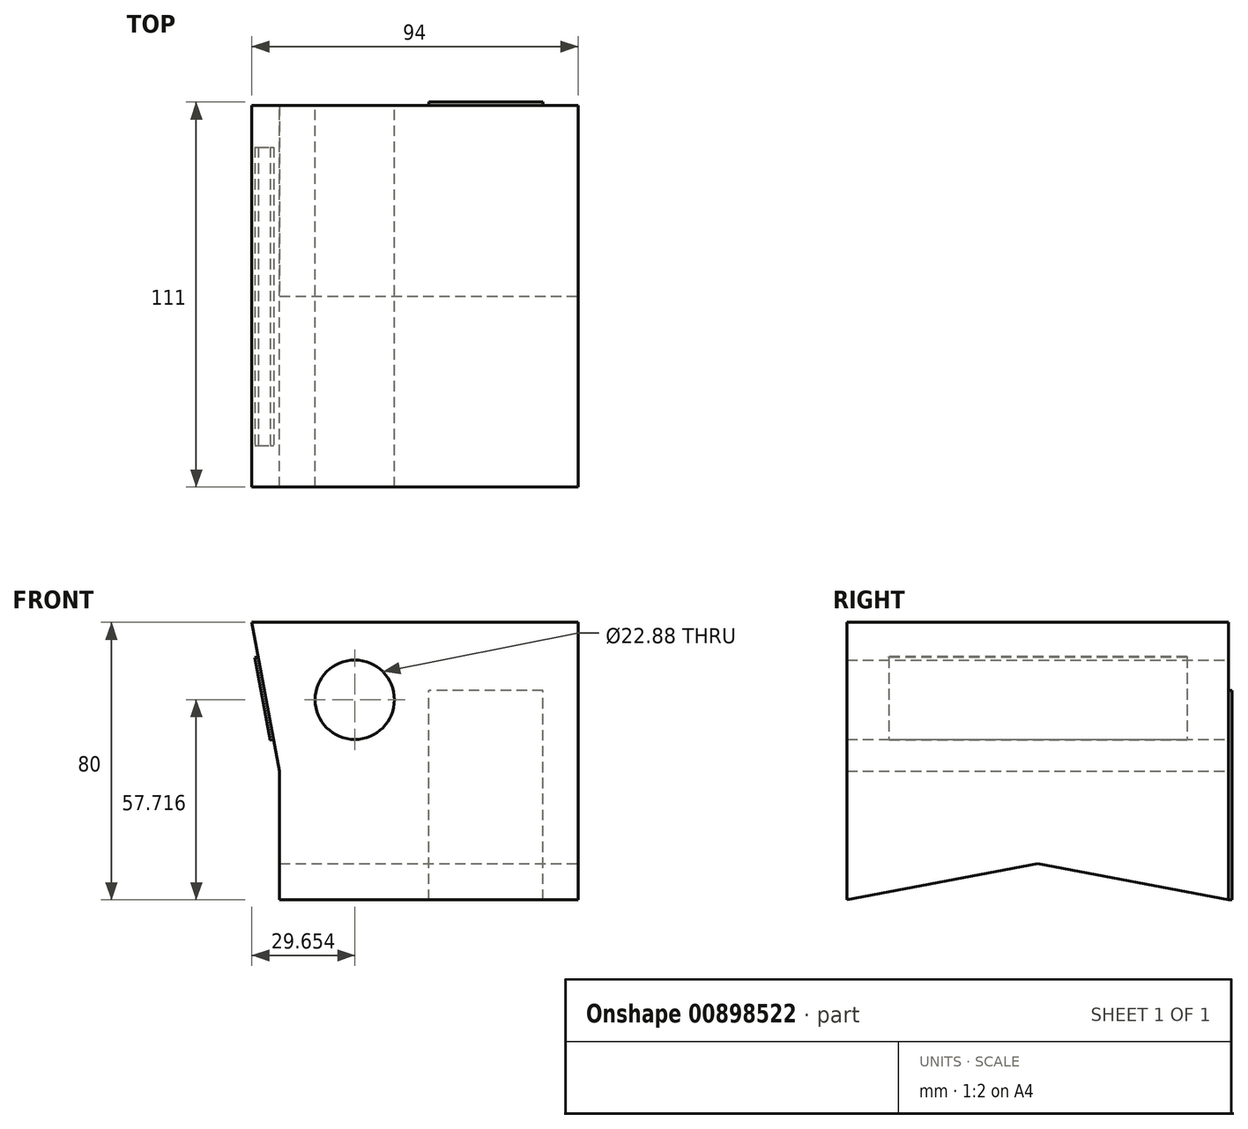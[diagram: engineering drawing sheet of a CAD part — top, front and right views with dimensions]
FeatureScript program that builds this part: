
annotation { "Feature Type Name" : "Feature", "Feature Type Description" : "" }
export const myFeature = defineFeature(function(context is Context, id is Id, definition is map)
    precondition{}
    {
        {
            var Q0;
            Q0=qCreatedBy(makeId("Front.planeOp"),FACE);
            var sketch = newSketch(context, id + "F0", { "sketchPlane" : qUnion([Q0])});
            skLineSegment(sketch, "E0.bottom", {"start": v(0, 0) * mm, "end": v(-80, 0) * mm});
            skLineSegment(sketch, "E0.top", {"start": v(0, 80) * mm, "end": v(-80, 80) * mm});
            skLineSegment(sketch, "E0.left", {"start": v(0, 0) * mm, "end": v(0, 80) * mm});
            skLineSegment(sketch, "E0.right", {"start": v(-80, 0) * mm, "end": v(-80, 80) * mm});
            skLineSegment(sketch, "E1", {"start": v(-80, 80) * mm, "end": v(-88, 80) * mm});
            skLineSegment(sketch, "E2", {"start": v(-88, 80) * mm, "end": v(-80, 37.1) * mm});
            skSolve(sketch);
        }
        {
            var Q0;
            {var subQ0=sQuery(id+"F0.wireOp",EDGE,"E1");Q0=makeQuery(id+"F0.imprint","IMPRINT",FACE,{"disambiguationData":[TD([[makeQuery(id+"F0.imprint","IMPRINT",EDGE,{"derivedFrom":subQ0}),1.0]])]});}
            var Q1;
            {var subQ1=sQuery(id+"F0.wireOp",EDGE,"E0.bottom");Q1=makeQuery(id+"F0.imprint","IMPRINT",FACE,{"disambiguationData":[TD([[makeQuery(id+"F0.imprint","IMPRINT",EDGE,{"derivedFrom":subQ1}),-1.0]])]});}
            extrude(context, id + "F1", {"entities" : qUnion([Q0, Q1]), "depth" : 6 * mm, "offsetDistance" : 25 * mm});
        }
        {
            var Q0;
            Q0=makeQuery(id+"F1.opExtrude","SWEPT_FACE",FACE,{"disambiguationData":[OSD([sQuery(id+"F0.wireOp",EDGE,"E0.left")])]});
            var sketch = newSketch(context, id + "F2", { "sketchPlane" : qUnion([Q0])});
            skLineSegment(sketch, "E3.bottom", {"start": v(-6, 0) * mm, "end": v(104, 0) * mm});
            skLineSegment(sketch, "E3.top", {"start": v(-6, 80) * mm, "end": v(104, 80) * mm});
            skLineSegment(sketch, "E3.left", {"start": v(-6, 0) * mm, "end": v(-6, 80) * mm});
            skLineSegment(sketch, "E3.right", {"start": v(104, 0) * mm, "end": v(104, 80) * mm});
            skSolve(sketch);
        }
        {
            var Q0;
            {var subQ2=sQuery(id+"F2.wireOp",EDGE,"E3.right");Q0=makeQuery(id+"F2.imprint","IMPRINT",FACE,{"disambiguationData":[TD([[makeQuery(id+"F2.imprint","IMPRINT",EDGE,{"derivedFrom":subQ2}),1.0]])]});}
            var Q1;
            {var subQ2=sQuery(id+"F2.wireOp",EDGE,"E3.left");Q1=makeQuery(id+"F2.imprint","IMPRINT",FACE,{"disambiguationData":[TD([[makeQuery(id+"F2.imprint","IMPRINT",EDGE,{"derivedFrom":subQ2}),-1.0]])]});}
            extrude(context, id + "F3", {"entities" : qUnion([Q0, Q1]), "operationType" : NewBodyOperationType.ADD, "depth" : 6 * mm, "offsetDistance" : 25 * mm});
        }
        {
            var Q0;
            Q0=makeQuery(id+"F3.boolean.opBoolean","MERGE",FACE,{"derivedFrom":[makeQuery(id+"F1.opExtrude","CAP_FACE",FACE,{"disambiguationData":[OSD([sQuery(id+"F0.wireOp",EDGE,"E0.bottom"),sQuery(id+"F0.wireOp",EDGE,"E0.top"),sQuery(id+"F0.wireOp",EDGE,"E0.left"),sQuery(id+"F0.wireOp",EDGE,"E0.right"),sQuery(id+"F0.wireOp",EDGE,"E1"),sQuery(id+"F0.wireOp",EDGE,"E2")])],"isStart":false}),makeQuery(id+"F3.opExtrude","SWEPT_FACE",FACE,{"disambiguationData":[OSD([sQuery(id+"F2.wireOp",EDGE,"E3.left")])]})]});
            var sketch = newSketch(context, id + "F4", { "sketchPlane" : qUnion([Q0])});
            skLineSegment(sketch, "E4", {"start": v(0, 80) * mm, "end": v(0, 0) * mm});
            skSolve(sketch);
        }
        {
            var Q0;
            Q0=makeQuery(id+"F1.opExtrude","CAP_FACE",FACE,{"disambiguationData":[OSD([sQuery(id+"F0.wireOp",EDGE,"E0.bottom"),sQuery(id+"F0.wireOp",EDGE,"E0.top"),sQuery(id+"F0.wireOp",EDGE,"E0.left"),sQuery(id+"F0.wireOp",EDGE,"E0.right"),sQuery(id+"F0.wireOp",EDGE,"E1"),sQuery(id+"F0.wireOp",EDGE,"E2")])],"isStart":true});
            var Q1;
            Q1=makeQuery(id+"F3.opExtrude","SWEPT_FACE",FACE,{"disambiguationData":[OSD([sQuery(id+"F2.wireOp",EDGE,"E3.right")])]});
            extrude(context, id + "F5", {"entities" : qUnion([Q0]), "operationType" : NewBodyOperationType.ADD, "endBound" : BoundingType.UP_TO_SURFACE, "depth" : 25 * mm, "endBoundEntityFace" : qUnion([Q1]), "offsetDistance" : 25 * mm});
        }
        {
            var Q0;
            Q0=makeQuery(id+"F3.opExtrude","CAP_FACE",FACE,{"disambiguationData":[OSD([sQuery(id+"F2.wireOp",EDGE,"E3.bottom"),sQuery(id+"F2.wireOp",EDGE,"E3.top"),sQuery(id+"F2.wireOp",EDGE,"E3.left"),sQuery(id+"F2.wireOp",EDGE,"E3.right")])],"isStart":false});
            var sketch = newSketch(context, id + "F6", { "sketchPlane" : qUnion([Q0])});
            skLineSegment(sketch, "E5", {"start": v(49, 10.5) * mm, "end": v(104, 0) * mm});
            skLineSegment(sketch, "E6", {"start": v(49, 10.5) * mm, "end": v(-6, 0) * mm});
            skSolve(sketch);
        }
        {
            var Q0;
            Q0=makeQuery(id+"F6.imprint","IMPRINT",FACE,{"disambiguationData":[TD([[makeQuery(id+"F6.imprint","IMPRINT",EDGE,{"derivedFrom":sQuery(id+"F6.wireOp",EDGE,"E5")}),-1.0]])]});
            extrude(context, id + "F7", {"entities" : qUnion([Q0]), "operationType" : NewBodyOperationType.REMOVE, "oppositeDirection" : true, "depth" : 200 * mm, "offsetDistance" : 25 * mm});
        }
        {
            var Q0;
            Q0=makeQuery(id+"F5.boolean.opBoolean","MERGE",FACE,{"derivedFrom":[makeQuery(id+"F3.opExtrude","SWEPT_FACE",FACE,{"disambiguationData":[OSD([sQuery(id+"F2.wireOp",EDGE,"E3.right")])]}),makeQuery(id+"F5.opExtrude","CAP_FACE",FACE,{"disambiguationData":[OSD([sQuery(id+"F0.wireOp",EDGE,"E0.bottom"),sQuery(id+"F0.wireOp",EDGE,"E0.top"),sQuery(id+"F0.wireOp",EDGE,"E0.left"),sQuery(id+"F0.wireOp",EDGE,"E0.right"),sQuery(id+"F0.wireOp",EDGE,"E1"),sQuery(id+"F0.wireOp",EDGE,"E2")])],"isStart":false})]});
            var sketch = newSketch(context, id + "F8", { "sketchPlane" : qUnion([Q0])});
            skLineSegment(sketch, "E7", {"start": v(0, 80) * mm, "end": v(0, 0) * mm});
            skLineSegment(sketch, "E8", {"start": v(85.12, 64.56) * mm, "end": v(79.22, 65.66) * mm});
            skLineSegment(sketch, "E9", {"start": v(79.22, 65.66) * mm, "end": v(81.9, 80) * mm});
            skLineSegment(sketch, "E10", {"start": v(80, 0) * mm, "end": v(74, 0) * mm});
            skLineSegment(sketch, "E11", {"start": v(74, 0) * mm, "end": v(74, 37.65) * mm});
            skLineSegment(sketch, "E12", {"start": v(74, 37.65) * mm, "end": v(81.9, 80) * mm});
            skLineSegment(sketch, "E13.bottom", {"start": v(8.37, 0) * mm, "end": v(39.44, 0) * mm});
            skLineSegment(sketch, "E13.top", {"start": v(8.37, 63.48) * mm, "end": v(39.44, 63.48) * mm});
            skLineSegment(sketch, "E13.left", {"start": v(8.37, 0) * mm, "end": v(8.37, 63.48) * mm});
            skLineSegment(sketch, "E13.right", {"start": v(39.44, 0) * mm, "end": v(39.44, 63.48) * mm});
            skCircle(sketch, "E14", {"center": v(58.35, 57.72) * mm, "radius": 11.44 * mm});
            skSolve(sketch);
        }
        {
            var Q0;
            Q0=makeQuery(id+"F3.opExtrude","CAP_FACE",FACE,{"disambiguationData":[OSD([sQuery(id+"F2.wireOp",EDGE,"E3.bottom"),sQuery(id+"F2.wireOp",EDGE,"E3.top"),sQuery(id+"F2.wireOp",EDGE,"E3.left"),sQuery(id+"F2.wireOp",EDGE,"E3.right")])],"isStart":false});
            var sketch = newSketch(context, id + "F9", { "sketchPlane" : qUnion([Q0])});
            skLineSegment(sketch, "E15.bottom", {"start": v(-6, 80) * mm, "end": v(6, 80) * mm});
            skLineSegment(sketch, "E15.left", {"start": v(-6, 80) * mm, "end": v(-6, 70) * mm});
            skLineSegment(sketch, "E16.bottom", {"start": v(104, 80) * mm, "end": v(92, 80) * mm});
            skLineSegment(sketch, "E16.left", {"start": v(104, 80) * mm, "end": v(104, 70) * mm});
            skLineSegment(sketch, "E17.bottom", {"start": v(5.82, 70) * mm, "end": v(92, 70) * mm});
            skLineSegment(sketch, "E17.top", {"start": v(5.82, 46.24) * mm, "end": v(92, 46.24) * mm});
            skLineSegment(sketch, "E17.left", {"start": v(5.82, 70) * mm, "end": v(5.82, 46.24) * mm});
            skLineSegment(sketch, "E17.right", {"start": v(92, 70) * mm, "end": v(92, 46.24) * mm});
            skLineSegment(sketch, "E18", {"start": v(48.9, 70) * mm, "end": v(53.9, 70) * mm});
            skLineSegment(sketch, "E19", {"start": v(43.9, 70) * mm, "end": v(43.9, 46.24) * mm});
            skLineSegment(sketch, "E20", {"start": v(53.9, 70) * mm, "end": v(53.9, 46.24) * mm});
            skSolve(sketch);
        }
        {
            var Q0;
            Q0=makeQuery(id+"F8.imprint","IMPRINT",FACE,{"disambiguationData":[TD([[makeQuery(id+"F8.imprint","IMPRINT",EDGE,{"derivedFrom":sQuery(id+"F8.wireOp",EDGE,"E14")}),1.0]])]});
            extrude(context, id + "F10", {"entities" : qUnion([Q0]), "operationType" : NewBodyOperationType.REMOVE, "oppositeDirection" : true, "depth" : 200 * mm, "offsetDistance" : 25 * mm});
        }
        {
            var Q0;
            {var subQ0=sQuery(id+"F0.wireOp",EDGE,"E2");Q0=makeQuery(id+"F5.boolean.opBoolean","MERGE",FACE,{"derivedFrom":[makeQuery(id+"F1.opExtrude","SWEPT_FACE",FACE,{"disambiguationData":[OSD([subQ0])]}),makeQuery(id+"F5.opExtrude","SWEPT_FACE",FACE,{"disambiguationData":[OSD([subQ0])]})]});}
            var sketch = newSketch(context, id + "F11", { "sketchPlane" : qUnion([Q0])});
            skLineSegment(sketch, "E21.bottom", {"start": v(-92, 84.7) * mm, "end": v(-6, 84.7) * mm});
            skLineSegment(sketch, "E21.top", {"start": v(-92, 60.4) * mm, "end": v(-6, 60.4) * mm});
            skLineSegment(sketch, "E21.left", {"start": v(-92, 84.7) * mm, "end": v(-92, 60.4) * mm});
            skLineSegment(sketch, "E21.right", {"start": v(-6, 84.7) * mm, "end": v(-6, 60.4) * mm});
            skSolve(sketch);
        }
        {
            var Q0;
            Q0=makeQuery(id+"F11.imprint","IMPRINT",FACE,{"disambiguationData":[TD([[makeQuery(id+"F11.imprint","IMPRINT",EDGE,{"derivedFrom":sQuery(id+"F11.wireOp",EDGE,"E21.bottom")}),-1.0]])]});
            extrude(context, id + "F12", {"entities" : qUnion([Q0]), "operationType" : NewBodyOperationType.ADD, "depth" : 1 * mm, "offsetDistance" : 25 * mm});
        }
        {
            var Q0;
            Q0=makeQuery(id+"F5.boolean.opBoolean","MERGE",FACE,{"derivedFrom":[makeQuery(id+"F3.opExtrude","SWEPT_FACE",FACE,{"disambiguationData":[OSD([sQuery(id+"F2.wireOp",EDGE,"E3.right")])]}),makeQuery(id+"F5.opExtrude","CAP_FACE",FACE,{"disambiguationData":[OSD([sQuery(id+"F0.wireOp",EDGE,"E0.bottom"),sQuery(id+"F0.wireOp",EDGE,"E0.top"),sQuery(id+"F0.wireOp",EDGE,"E0.left"),sQuery(id+"F0.wireOp",EDGE,"E0.right"),sQuery(id+"F0.wireOp",EDGE,"E1"),sQuery(id+"F0.wireOp",EDGE,"E2")])],"isStart":false})]});
            var sketch = newSketch(context, id + "F13", { "sketchPlane" : qUnion([Q0])});
            skLineSegment(sketch, "E22.bottom", {"start": v(4.1, 0) * mm, "end": v(36.94, 0) * mm});
            skLineSegment(sketch, "E22.top", {"start": v(4.1, 60.4) * mm, "end": v(36.94, 60.4) * mm});
            skLineSegment(sketch, "E22.left", {"start": v(4.1, 0) * mm, "end": v(4.1, 60.4) * mm});
            skLineSegment(sketch, "E22.right", {"start": v(36.94, 0) * mm, "end": v(36.94, 60.4) * mm});
            skSolve(sketch);
        }
        {
            var Q0;
            Q0=makeQuery(id+"F13.imprint","IMPRINT",FACE,{"disambiguationData":[TD([[makeQuery(id+"F13.imprint","IMPRINT",EDGE,{"derivedFrom":sQuery(id+"F13.wireOp",EDGE,"E22.bottom")}),1.0]])]});
            extrude(context, id + "F14", {"entities" : qUnion([Q0]), "operationType" : NewBodyOperationType.ADD, "depth" : 1 * mm, "offsetDistance" : 25 * mm});
        }
    });
